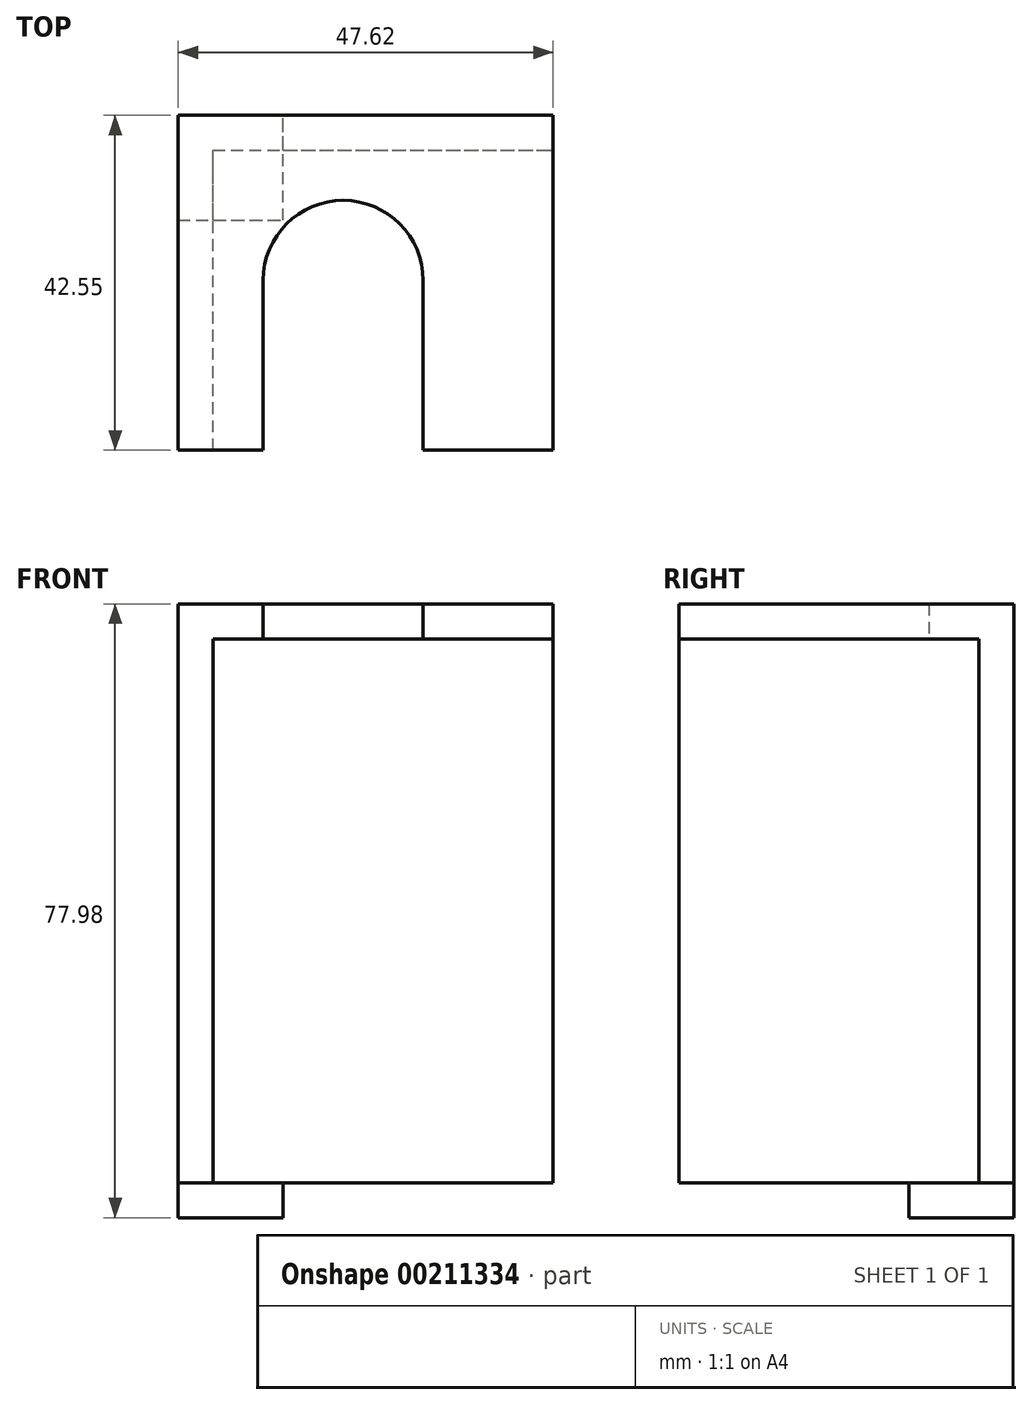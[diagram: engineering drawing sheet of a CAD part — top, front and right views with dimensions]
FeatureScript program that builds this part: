
annotation { "Feature Type Name" : "Feature", "Feature Type Description" : "" }
export const myFeature = defineFeature(function(context is Context, id is Id, definition is map)
    precondition{}
    {
        {
            var Q0;
            Q0=qCreatedBy(makeId("Front.planeOp"),FACE);
            var sketch = newSketch(context, id + "F0", { "sketchPlane" : qUnion([Q0])});
            skLineSegment(sketch, "E0.bottom", {"start": v(0, 0) * mm, "end": v(4.45, 0) * mm});
            skLineSegment(sketch, "E0.top", {"start": v(0, 69.09) * mm, "end": v(4.44, 69.09) * mm});
            skLineSegment(sketch, "E0.left", {"start": v(0, 0) * mm, "end": v(0, 69.09) * mm});
            skLineSegment(sketch, "E0.right", {"start": v(4.45, 0) * mm, "end": v(4.45, 69.09) * mm});
            skSolve(sketch);
        }
        {
            var Q0;
            Q0 = qSketchRegion(id + "F0", true);
            extrude(context, id + "F1", {"entities" : qUnion([Q0]), "depth" : 42.55 * mm});
        }
        {
            var Q0;
            Q0=qCreatedBy(makeId("Front.planeOp"),FACE);
            var sketch = newSketch(context, id + "F2", { "sketchPlane" : qUnion([Q0])});
            skLineSegment(sketch, "E1.bottom", {"start": v(4.45, 0) * mm, "end": v(47.62, 0) * mm});
            skLineSegment(sketch, "E1.top", {"start": v(4.45, 69.09) * mm, "end": v(47.62, 69.09) * mm});
            skLineSegment(sketch, "E1.left", {"start": v(4.45, 0) * mm, "end": v(4.44, 69.09) * mm});
            skLineSegment(sketch, "E1.right", {"start": v(47.62, 0) * mm, "end": v(47.62, 69.09) * mm});
            skSolve(sketch);
        }
        {
            var Q0;
            Q0 = qSketchRegion(id + "F2", true);
            extrude(context, id + "F3", {"entities" : qUnion([Q0]), "operationType" : NewBodyOperationType.ADD, "depth" : 4.44 * mm});
        }
        {
            var Q0;
            Q0=qCreatedBy(makeId("Front.planeOp"),FACE);
            var sketch = newSketch(context, id + "F4", { "sketchPlane" : qUnion([Q0])});
            skLineSegment(sketch, "E2.bottom", {"start": v(0, 0) * mm, "end": v(13.33, 0) * mm});
            skLineSegment(sketch, "E2.top", {"start": v(0, -4.45) * mm, "end": v(13.33, -4.45) * mm});
            skLineSegment(sketch, "E2.left", {"start": v(0, 0) * mm, "end": v(0, -4.45) * mm});
            skLineSegment(sketch, "E2.right", {"start": v(13.33, 0) * mm, "end": v(13.33, -4.45) * mm});
            skSolve(sketch);
        }
        {
            var Q0;
            Q0 = qSketchRegion(id + "F4", true);
            extrude(context, id + "F5", {"entities" : qUnion([Q0]), "operationType" : NewBodyOperationType.ADD, "depth" : 13.33 * mm});
        }
        {
            var Q0;
            Q0=makeQuery(id+"F3.boolean.opBoolean","MERGE",FACE,{"derivedFrom":[makeQuery(id+"F1.opExtrude","SWEPT_FACE",FACE,{"disambiguationData":[OSD([sQuery(id+"F0.wireOp",EDGE,"E0.top")])]}),makeQuery(id+"F3.opExtrude","SWEPT_FACE",FACE,{"disambiguationData":[OSD([sQuery(id+"F2.wireOp",EDGE,"E1.top")])]})]});
            var sketch = newSketch(context, id + "F6", { "sketchPlane" : qUnion([Q0])});
            skLineSegment(sketch, "E3.bottom", {"start": v(0, 0) * mm, "end": v(47.62, 0) * mm});
            skLineSegment(sketch, "E3.top", {"start": v(0, -42.55) * mm, "end": v(10.8, -42.55) * mm});
            skLineSegment(sketch, "E3.left", {"start": v(0, 0) * mm, "end": v(0, -42.55) * mm});
            skLineSegment(sketch, "E3.right", {"start": v(47.62, 0) * mm, "end": v(47.62, -42.55) * mm});
            skArc(sketch, "E4", {"start": v(31.12, -20.96) * mm, "mid": v(20.96, -10.8) * mm, "end": v(10.8, -20.96) * mm});
            skLineSegment(sketch, "E5", {"start": v(10.8, -20.96) * mm, "end": v(10.8, -42.55) * mm});
            skLineSegment(sketch, "E6", {"start": v(31.12, -20.96) * mm, "end": v(31.12, -42.55) * mm});
            skLineSegment(sketch, "E7.trimOffspring", {"start": v(31.12, -42.55) * mm, "end": v(47.62, -42.55) * mm});
            skSolve(sketch);
        }
        {
            var Q0;
            Q0 = qSketchRegion(id + "F6", true);
            extrude(context, id + "F7", {"entities" : qUnion([Q0]), "operationType" : NewBodyOperationType.ADD, "depth" : 4.44 * mm});
        }
    });
